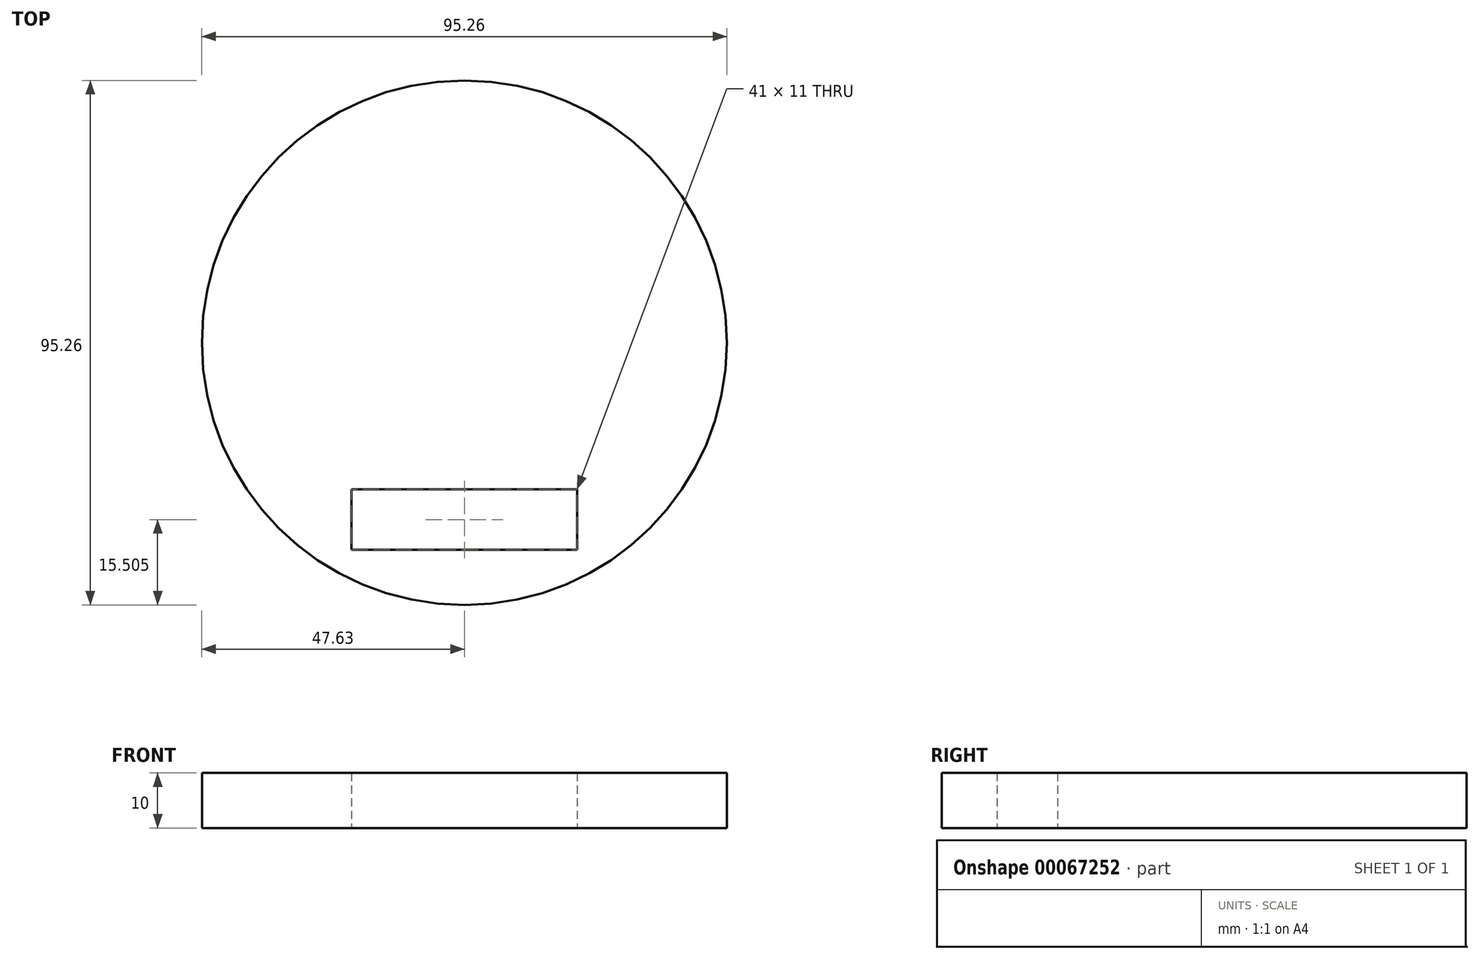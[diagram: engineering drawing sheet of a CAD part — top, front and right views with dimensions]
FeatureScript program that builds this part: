
annotation { "Feature Type Name" : "Feature", "Feature Type Description" : "" }
export const myFeature = defineFeature(function(context is Context, id is Id, definition is map)
    precondition{}
    {
        {
            var Q0;
            Q0=qCreatedBy(makeId("Top.planeOp"),FACE);
            var sketch = newSketch(context, id + "F0", { "sketchPlane" : qUnion([Q0])});
            skCircle(sketch, "E0", {"center": v(0, 0) * mm, "radius": 47.63 * mm});
            skLineSegment(sketch, "E1", {"start": v(20.5, -37.63) * mm, "end": v(-20.5, -37.63) * mm});
            skLineSegment(sketch, "E2", {"start": v(-20.5, -37.63) * mm, "end": v(-20.5, -26.63) * mm});
            skLineSegment(sketch, "E3", {"start": v(-20.5, -26.63) * mm, "end": v(20.5, -26.63) * mm});
            skLineSegment(sketch, "E4", {"start": v(20.5, -26.63) * mm, "end": v(20.5, -37.63) * mm});
            skSolve(sketch);
        }
        {
            var Q0;
            Q0=qSketchRegion(id+"F0",true);
            extrude(context, id + "F1", {"entities" : qUnion([Q0]), "depth" : 10 * mm});
        }
    });
